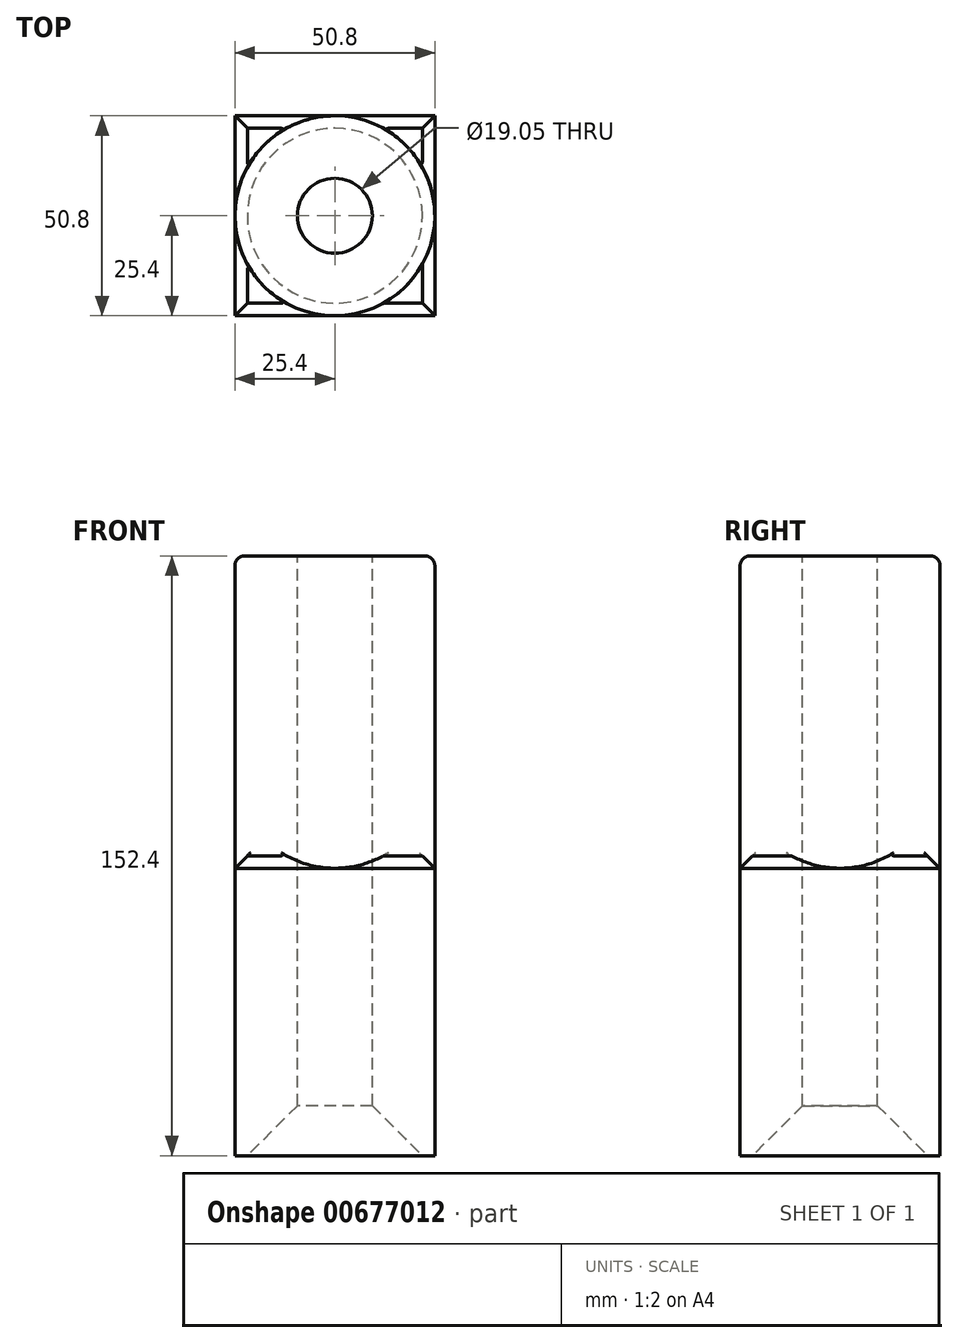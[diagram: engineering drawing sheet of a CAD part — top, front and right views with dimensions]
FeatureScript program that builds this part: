
annotation { "Feature Type Name" : "Feature", "Feature Type Description" : "" }
export const myFeature = defineFeature(function(context is Context, id is Id, definition is map)
    precondition{}
    {
        {
            var Q0;
            Q0=qCreatedBy(makeId("Front.planeOp"),FACE);
            var sketch = newSketch(context, id + "F0", { "sketchPlane" : qUnion([Q0])});
            skLineSegment(sketch, "E0.bottom", {"start": v(-25.4, 38.1) * mm, "end": v(25.4, 38.1) * mm});
            skLineSegment(sketch, "E0.top", {"start": v(-25.4, -38.1) * mm, "end": v(25.4, -38.1) * mm});
            skLineSegment(sketch, "E0.left", {"start": v(-25.4, 38.1) * mm, "end": v(-25.4, -38.1) * mm});
            skLineSegment(sketch, "E0.right", {"start": v(25.4, 38.1) * mm, "end": v(25.4, -38.1) * mm});
            skSolve(sketch);
        }
        {
            var Q0;
            Q0=makeQuery(id+"F0.imprint","IMPRINT",FACE,{"disambiguationData":[TD([[makeQuery(id+"F0.imprint","IMPRINT",EDGE,{"derivedFrom":sQuery(id+"F0.wireOp",EDGE,"E0.bottom")}),-1.0]])]});
            extrude(context, id + "F1", {"entities" : qUnion([Q0]), "depth" : 50.8 * mm, "offsetDistance" : 25.4 * mm});
        }
        {
            var Q0;
            Q0=makeQuery(id+"F1.opExtrude","SWEPT_FACE",FACE,{"disambiguationData":[OSD([sQuery(id+"F0.wireOp",EDGE,"E0.bottom")])]});
            var sketch = newSketch(context, id + "F2", { "sketchPlane" : qUnion([Q0])});
            skCircle(sketch, "E1", {"center": v(0, -25.4) * mm, "radius": 25.4 * mm});
            skSolve(sketch);
        }
        {
            var Q0;
            Q0 = qSketchRegion(id + "F2", true);
            extrude(context, id + "F3", {"entities" : qUnion([Q0]), "operationType" : NewBodyOperationType.ADD, "depth" : 76.2 * mm, "offsetDistance" : 25.4 * mm});
        }
        {
            var Q0;
            Q0=makeQuery(id+"F3.opExtrude","CAP_FACE",FACE,{"disambiguationData":[OSD([sQuery(id+"F2.wireOp",EDGE,"E1")])],"isStart":false});
            var sketch = newSketch(context, id + "F4", { "sketchPlane" : qUnion([Q0])});
            skCircle(sketch, "E2", {"center": v(0, -25.4) * mm, "radius": 9.53 * mm});
            skSolve(sketch);
        }
        {
            var Q0;
            Q0 = qSketchRegion(id + "F4", true);
            extrude(context, id + "F5", {"entities" : qUnion([Q0]), "operationType" : NewBodyOperationType.REMOVE, "endBound" : BoundingType.THROUGH_ALL, "oppositeDirection" : true, "depth" : 25.4 * mm, "offsetDistance" : 25.4 * mm});
        }
        {
            var Q0;
            Q0=makeQuery(id+"F3.opExtrude","CAP_EDGE",EDGE,{"disambiguationData":[OSD([sQuery(id+"F2.wireOp",EDGE,"E1")])],"isStart":false});
            fillet(context, id + "F6", {"entities" : qUnion([Q0]), "radius" : 2.54 * mm, "tangentPropagation" : true, "allowEdgeOverflow" : false});
        }
        {
            var Q0;
            {var subQ0=sQuery(id+"F0.wireOp",EDGE,"E0.bottom");var subQ1=sQuery(id+"F0.wireOp",EDGE,"E0.right");Q0=makeQuery(id+"F3.boolean.opBoolean","SPLIT",EDGE,{"disambiguationData":[TD([makeQuery(id+"F1.opExtrude","CAP_FACE",FACE,{"disambiguationData":[OSD([subQ0,sQuery(id+"F0.wireOp",EDGE,"E0.top"),sQuery(id+"F0.wireOp",EDGE,"E0.left"),subQ1])],"isStart":true})])],"derivedFrom":makeQuery(id+"F1.opExtrude","SWEPT_EDGE",EDGE,{"disambiguationData":[OSD([subQ0,subQ1])]})});}
            var Q1;
            {var subQ0=sQuery(id+"F0.wireOp",EDGE,"E0.bottom");var subQ1=sQuery(id+"F0.wireOp",EDGE,"E0.right");Q1=makeQuery(id+"F3.boolean.opBoolean","SPLIT",EDGE,{"disambiguationData":[TD([makeQuery(id+"F1.opExtrude","SWEPT_FACE",FACE,{"disambiguationData":[OSD([subQ1])]})])],"derivedFrom":makeQuery(id+"F1.opExtrude","CAP_EDGE",EDGE,{"disambiguationData":[OSD([subQ0])],"isStart":true})});}
            var Q2;
            {var subQ0=sQuery(id+"F0.wireOp",EDGE,"E0.bottom");var subQ1=sQuery(id+"F0.wireOp",EDGE,"E0.left");Q2=makeQuery(id+"F3.boolean.opBoolean","SPLIT",EDGE,{"disambiguationData":[TD([makeQuery(id+"F1.opExtrude","CAP_FACE",FACE,{"disambiguationData":[OSD([subQ0,sQuery(id+"F0.wireOp",EDGE,"E0.top"),subQ1,sQuery(id+"F0.wireOp",EDGE,"E0.right")])],"isStart":true})])],"derivedFrom":makeQuery(id+"F1.opExtrude","SWEPT_EDGE",EDGE,{"disambiguationData":[OSD([subQ0,subQ1])]})});}
            var Q3;
            {var subQ0=sQuery(id+"F0.wireOp",EDGE,"E0.bottom");var subQ1=sQuery(id+"F0.wireOp",EDGE,"E0.left");Q3=makeQuery(id+"F3.boolean.opBoolean","SPLIT",EDGE,{"disambiguationData":[TD([makeQuery(id+"F1.opExtrude","CAP_FACE",FACE,{"disambiguationData":[OSD([subQ0,sQuery(id+"F0.wireOp",EDGE,"E0.top"),subQ1,sQuery(id+"F0.wireOp",EDGE,"E0.right")])],"isStart":false})])],"derivedFrom":makeQuery(id+"F1.opExtrude","SWEPT_EDGE",EDGE,{"disambiguationData":[OSD([subQ0,subQ1])]})});}
            var Q4;
            {var subQ0=sQuery(id+"F0.wireOp",EDGE,"E0.bottom");var subQ1=sQuery(id+"F0.wireOp",EDGE,"E0.left");Q4=makeQuery(id+"F3.boolean.opBoolean","SPLIT",EDGE,{"disambiguationData":[TD([makeQuery(id+"F1.opExtrude","SWEPT_FACE",FACE,{"disambiguationData":[OSD([subQ1])]})])],"derivedFrom":makeQuery(id+"F1.opExtrude","CAP_EDGE",EDGE,{"disambiguationData":[OSD([subQ0])],"isStart":false})});}
            chamfer(context, id + "F7", {"entities" : qUnion([Q0, Q1, Q2, Q3, Q4]), "width" : 3.17 * mm, "tangentPropagation" : true});
        }
        {
            var Q0;
            {var subQ0=sQuery(id+"F0.wireOp",EDGE,"E0.bottom");var subQ1=sQuery(id+"F0.wireOp",EDGE,"E0.left");var subQ2=sQuery(id+"F2.wireOp",EDGE,"E1");Q0=makeQuery(id+"F3.boolean.opBoolean","SPLIT",EDGE,{"disambiguationData":[TD([makeQuery(id+"F1.opExtrude","SWEPT_FACE",FACE,{"disambiguationData":[OSD([subQ0])]}),makeQuery(id+"F1.opExtrude","CAP_FACE",FACE,{"disambiguationData":[OSD([subQ0,sQuery(id+"F0.wireOp",EDGE,"E0.top"),subQ1,sQuery(id+"F0.wireOp",EDGE,"E0.right")])],"isStart":true}),makeQuery(id+"F1.opExtrude","SWEPT_FACE",FACE,{"disambiguationData":[OSD([subQ1])]}),makeQuery(id+"F3.opExtrude","SWEPT_FACE",FACE,{"disambiguationData":[OSD([subQ2])]})])],"derivedFrom":makeQuery(id+"F3.opExtrude","CAP_EDGE",EDGE,{"disambiguationData":[OSD([subQ2])],"isStart":true})});}
            var Q1;
            {var subQ0=sQuery(id+"F0.wireOp",EDGE,"E0.bottom");var subQ1=sQuery(id+"F0.wireOp",EDGE,"E0.left");var subQ2=sQuery(id+"F2.wireOp",EDGE,"E1");Q1=makeQuery(id+"F3.boolean.opBoolean","SPLIT",EDGE,{"disambiguationData":[TD([makeQuery(id+"F1.opExtrude","SWEPT_FACE",FACE,{"disambiguationData":[OSD([subQ0])]}),makeQuery(id+"F1.opExtrude","CAP_FACE",FACE,{"disambiguationData":[OSD([subQ0,sQuery(id+"F0.wireOp",EDGE,"E0.top"),subQ1,sQuery(id+"F0.wireOp",EDGE,"E0.right")])],"isStart":false}),makeQuery(id+"F1.opExtrude","SWEPT_FACE",FACE,{"disambiguationData":[OSD([subQ1])]}),makeQuery(id+"F3.opExtrude","SWEPT_FACE",FACE,{"disambiguationData":[OSD([subQ2])]})])],"derivedFrom":makeQuery(id+"F3.opExtrude","CAP_EDGE",EDGE,{"disambiguationData":[OSD([subQ2])],"isStart":true})});}
            var Q2;
            {var subQ0=sQuery(id+"F0.wireOp",EDGE,"E0.bottom");var subQ1=sQuery(id+"F0.wireOp",EDGE,"E0.right");var subQ2=sQuery(id+"F2.wireOp",EDGE,"E1");Q2=makeQuery(id+"F3.boolean.opBoolean","SPLIT",EDGE,{"disambiguationData":[TD([makeQuery(id+"F1.opExtrude","SWEPT_FACE",FACE,{"disambiguationData":[OSD([subQ0])]}),makeQuery(id+"F1.opExtrude","CAP_FACE",FACE,{"disambiguationData":[OSD([subQ0,sQuery(id+"F0.wireOp",EDGE,"E0.top"),sQuery(id+"F0.wireOp",EDGE,"E0.left"),subQ1])],"isStart":false}),makeQuery(id+"F1.opExtrude","SWEPT_FACE",FACE,{"disambiguationData":[OSD([subQ1])]}),makeQuery(id+"F3.opExtrude","SWEPT_FACE",FACE,{"disambiguationData":[OSD([subQ2])]})])],"derivedFrom":makeQuery(id+"F3.opExtrude","CAP_EDGE",EDGE,{"disambiguationData":[OSD([subQ2])],"isStart":true})});}
            var Q3;
            {var subQ0=sQuery(id+"F0.wireOp",EDGE,"E0.bottom");var subQ1=sQuery(id+"F0.wireOp",EDGE,"E0.right");var subQ2=sQuery(id+"F2.wireOp",EDGE,"E1");Q3=makeQuery(id+"F3.boolean.opBoolean","SPLIT",EDGE,{"disambiguationData":[TD([makeQuery(id+"F1.opExtrude","SWEPT_FACE",FACE,{"disambiguationData":[OSD([subQ0])]}),makeQuery(id+"F1.opExtrude","CAP_FACE",FACE,{"disambiguationData":[OSD([subQ0,sQuery(id+"F0.wireOp",EDGE,"E0.top"),sQuery(id+"F0.wireOp",EDGE,"E0.left"),subQ1])],"isStart":true}),makeQuery(id+"F1.opExtrude","SWEPT_FACE",FACE,{"disambiguationData":[OSD([subQ1])]}),makeQuery(id+"F3.opExtrude","SWEPT_FACE",FACE,{"disambiguationData":[OSD([subQ2])]})])],"derivedFrom":makeQuery(id+"F3.opExtrude","CAP_EDGE",EDGE,{"disambiguationData":[OSD([subQ2])],"isStart":true})});}
            fillet(context, id + "F8", {"entities" : qUnion([Q0, Q1, Q2, Q3]), "radius" : 0.76 * mm, "tangentPropagation" : true, "allowEdgeOverflow" : false});
        }
        {
            var Q0;
            Q0=makeQuery(id+"F5.boolean.opBoolean","INTERSECT",EDGE,{"derivedFrom":[makeQuery(id+"F1.opExtrude","SWEPT_FACE",FACE,{"disambiguationData":[OSD([sQuery(id+"F0.wireOp",EDGE,"E0.top")])]}),makeQuery(id+"F5.opExtrude","SWEPT_FACE",FACE,{"disambiguationData":[OSD([sQuery(id+"F4.wireOp",EDGE,"E2")])]})]});
            chamfer(context, id + "F9", {"entities" : qUnion([Q0]), "width" : 12.7 * mm, "tangentPropagation" : true});
        }
    });
